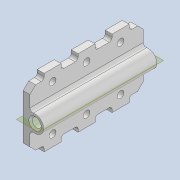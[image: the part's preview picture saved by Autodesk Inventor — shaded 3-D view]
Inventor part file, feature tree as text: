
AUTODESK INVENTOR PART (.ipt)
format: ipt  version: 2020 (Build 240168000, 168)  size: 210,944 bytes
history: native  units: mm
features: extrude x3, sketch x3, other x3, fillet x2, chamfer x2, projected_geometry x2, plane x1, mirror x1, reference x1
ambient origin geometry x8: Origin, YZ Plane, XZ Plane, XY Plane, X Axis, Y Axis, Z Axis, Center Point
bodies: Solid1 (feature_tree)
feature tree (18):
  extrude  "Extrusion1"  Depth=3.0mm
  fillet  "Fillet1"  Radius=1.2mm
  chamfer  "Chamfer1"  Distance=20.0mm
  extrude  "Extrusion2"  Depth=0.3mm TaperAngle=45.0deg
  extrude  "Extrusion3"  Depth=1.0mm
  plane  "Work Plane1"
  mirror  "Mirror1"
  fillet  "Fillet2"  Radius=4.0mm
  chamfer  "Chamfer2"  Distance=6.0mm
  sketch  "Sketch1"  dims[d0=1.6mm d1=3.0mm d2=1.2mm]
  reference  "Reference1"
  sketch  "Sketch2"  dims[d3=10.0mm d4=20.0mm d5=0.0mm]
  projected_geometry  "Projected Loop1"
  sketch  "Sketch3"  dims[d6=0.5mm d7=0.3mm d8=2.0mm d9=45.0deg d10=1.0mm d11=4.0mm d12=6.0mm d13=6.0mm d14=1.2mm d15=1.2mm d16=1.2mm d17=20.0mm d18=0.0mm d19=4.0mm d20=3.0mm d21=4.0mm d22=3.0mm d23=4.0mm d24=3.0mm d25=20.0mm d26=0.0mm d27=0.5mm d28=1.0mm d29=2.0mm d30=45.0deg]
  projected_geometry  "Projected Loop2"
  parser-record x1  (decoder bookkeeping rows leaked as tree rows — omitted from the tree; the rows remain in map.json)
  other  "bl_tube_ass_2.iam"
  other  "bw_tube_0.8_1.6:1"
note: 1 file-system path scrubbed to <path> (originals preserved in map.json)
